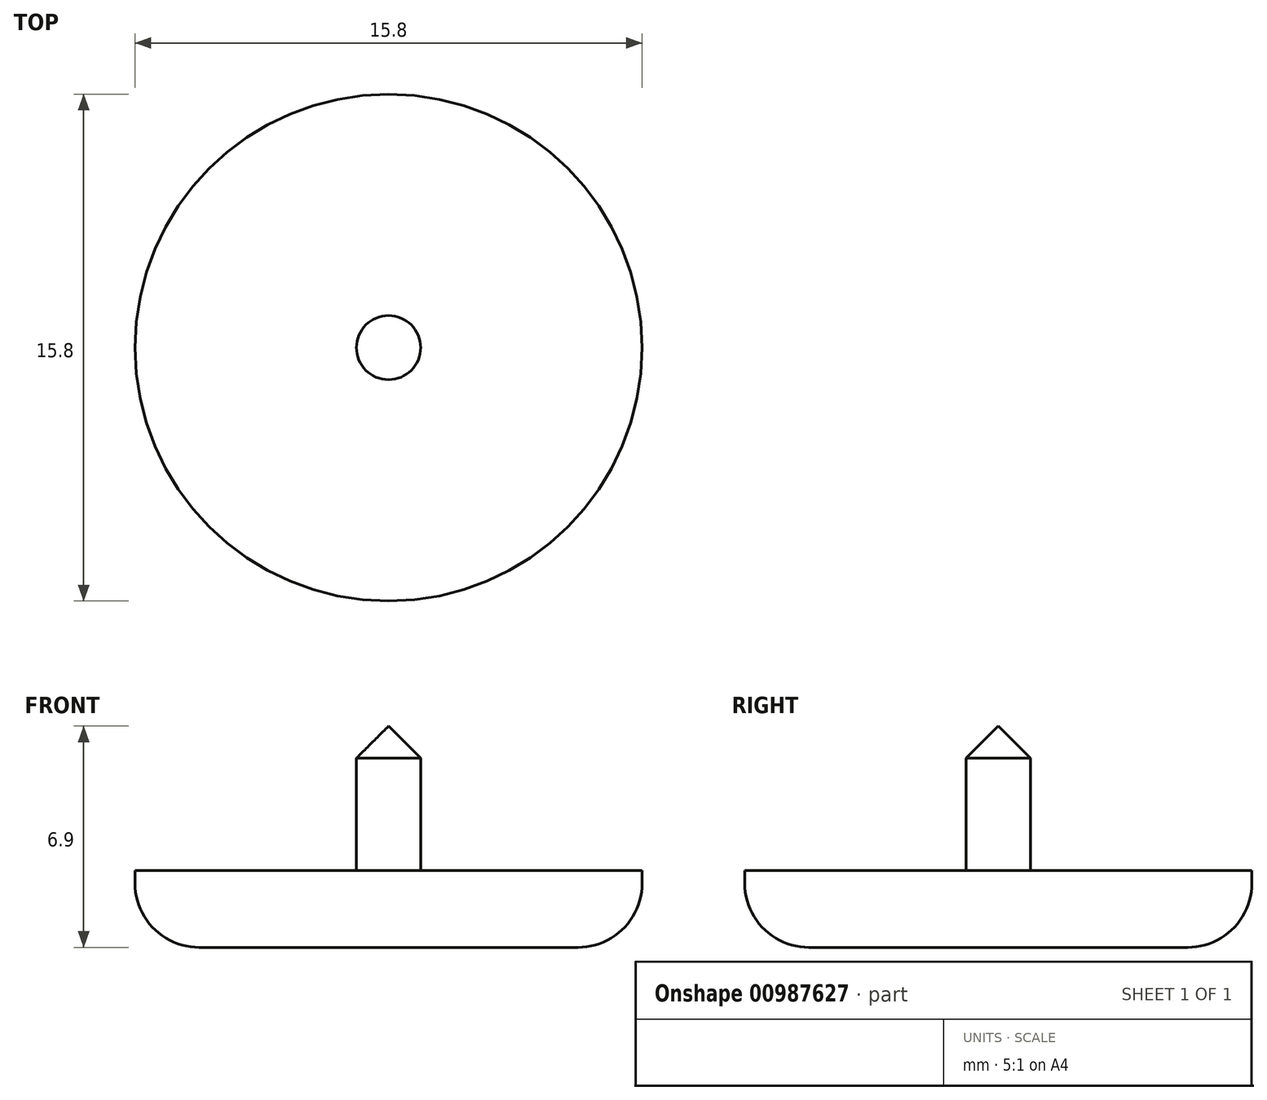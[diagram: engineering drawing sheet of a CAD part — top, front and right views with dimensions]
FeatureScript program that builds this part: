
annotation { "Feature Type Name" : "Feature", "Feature Type Description" : "" }
export const myFeature = defineFeature(function(context is Context, id is Id, definition is map)
    precondition{}
    {
        {
            var Q0;
            Q0=qCreatedBy(makeId("Top.planeOp"),FACE);
            var sketch = newSketch(context, id + "F0", { "sketchPlane" : qUnion([Q0])});
            skCircle(sketch, "E0", {"center": v(0, 0) * mm, "radius": 7.9 * mm});
            skSolve(sketch);
        }
        {
            var Q0;
            Q0 = qSketchRegion(id + "F0", true);
            extrude(context, id + "F1", {"entities" : qUnion([Q0]), "oppositeDirection" : true, "depth" : 2.4 * mm, "offsetDistance" : 25 * mm});
        }
        {
            var Q0;
            Q0=makeQuery(id+"F1.opExtrude","CAP_FACE",FACE,{"disambiguationData":[OSD([sQuery(id+"F0.wireOp",EDGE,"E0")])],"isStart":true});
            var sketch = newSketch(context, id + "F2", { "sketchPlane" : qUnion([Q0])});
            skCircle(sketch, "E1", {"center": v(0, 0) * mm, "radius": 1 * mm});
            skSolve(sketch);
        }
        {
            var Q0;
            Q0 = qSketchRegion(id + "F2", true);
            extrude(context, id + "F3", {"entities" : qUnion([Q0]), "operationType" : NewBodyOperationType.ADD, "depth" : 4.5 * mm, "offsetDistance" : 25 * mm});
        }
        {
            var Q0;
            Q0=makeQuery(id+"F1.opExtrude","CAP_EDGE",EDGE,{"disambiguationData":[OSD([sQuery(id+"F0.wireOp",EDGE,"E0")])],"isStart":false});
            fillet(context, id + "F4", {"entities" : qUnion([Q0]), "radius" : 2 * mm, "tangentPropagation" : true, "allowEdgeOverflow" : false});
        }
        {
            var Q0;
            Q0=makeQuery(id+"F3.opExtrude","CAP_EDGE",EDGE,{"disambiguationData":[OSD([sQuery(id+"F2.wireOp",EDGE,"E1")])],"isStart":false});
            chamfer(context, id + "F5", {"entities" : qUnion([Q0]), "width" : 1 * mm, "tangentPropagation" : true});
        }
    });
